# Revit family: WC Seat IS_SoftMood_Multiproduct_BIM_GB;T6391;T6392
name_source: partatom
category: Plumbing Fixtures
revit_build: Autodesk Revit MEP 2012 (Build: 20110309_2315(x64)
units: mm (PartAtom-declared; Revit-internal decimal feet)

## types (2) — shared parameters
AreaUnits = millimeters
Assembly Code = C1030200
AssetType = Fixed
BREEAM Approved = Yes
Brand = Ideal Standard
ConnectionType = Plumbing
CurrentRevision = 1
Default Elevation = 1219 mm
DurationUnit = year
ECA = Yes
ElementType = TOILETPAN: Soil appliance for the disposal of excrement
ExpectedLife = 15
Finish = White
InstallationInstructions = www.idealspec.co.uk/resources.html
LinearUnits = millimeters
ManufacturerURL = www.idealspec.co.uk
NBSDescription = WC seats and covers
NBSReference = 45-35-70/391
NettWeight = 2.7 Kg
NominalHeight = 40 mm
NominalLength = 443 mm
NominalWidth = 360 mm
Shape = Ring
Space = Internal
SpareParts = www.fastpart-spares.co.uk
ToiletPanType = WashDown
ToiletType = Other
URL = www.idealspec.co.uk
Uniclass2 = Pr_40_20_93_95
Version = 1
VolumeUnits = Litres
WRAS = Yes
WarrantyDescription = Manufacturers Warranty
WarrantyDurationParts = 5
WarrantyDurationUnit = year
WaterEfficientProduct = Yes
zero-valued in all types: CWFU, HWFU, WFU

## per-type parameters (varying)
| type | BIMObjectName | Description | Features | Model | ModelNumber | ModelReference | Name | NominalDepth | ProductInformation |
| T6391-Softmood Normal Seat And Cover | ISI_IdealStandard_WCSeats_Softmood_T639101 | Softmood normal seat and cover | Seat and cover | T639101 | T639101 | Softmood normal seat and cover | WCSeats_Softmood_T639101_IdealStandard | 0 | www.idealspec.co.uk/assets/datasheet/T639101 |
| T6392-Softmood Soft Close Seat And Cover | ISI_IdealStandard_WCSeats_Softmood_T639201 | Softmood soft close seat and cover | Soft close seat and cover | T639201 | T639201 | Softmood soft close seat and cover | WCSeats_Softmood_T639201_IdealStandard | 443 | www.idealspec.co.uk/assets/datasheet/T639201 |

## geometry (parser evidence)
native form markers: Sweep x2
no freeform markers — native parametric forms only
